# Revit family: 130411-00520
name_source: partatom
category: Обобщенные модели
units: mm (PartAtom-declared; Revit-internal decimal feet)

## family parameters
Всегда вертикально = Да
Может служить основой для арматурных стержней = Нет
На основе рабочей плоскости = Нет
Общий = Нет
При загрузке вырезать с полостями = Нет
Размер круглого соединителя = Использовать диаметр
Тип детали = Нормальный
Точка расчета площади = Нет

## types (1)
- ШТ-НП-33U-600-600-М
    ADSK_URL страницы изделия = https://www.ssd.ru
    ADSK_Единица измерения = шт
    ADSK_Завод-изготовитель = АО СВЯЗЬСТРОЙДЕТАЛЬ
    ADSK_Зона = -
    ADSK_Код изделия = 130411-00520
    ADSK_Масса_Текст = 71
    ADSK_Наименование = Шкаф телекоммуникационный напольный 19 33U(600x600) ШТ-НП-33U-600-600-М передняя дверь металл ССД
    ADSK_Наименование краткое = ШТ-НП-33U-600-600-М
    ADSK_Обозначение = -
    ADSK_Предел огнестойкости = -
    ADSK_Размер_Высота = 1639 мм
    Материал каркаса = Металл белый
    Материал колес и ручек = Металл черный
    Материал крепежей = Металл
    Ноль = 0 мм
    Описание = Шкаф телекоммуникационный напольный 19 33U(600x600) ШТ-НП-33U-600-600-М передняя дверь металл ССД
    Тип шкафа = Дверь : Металическая дверь белая
